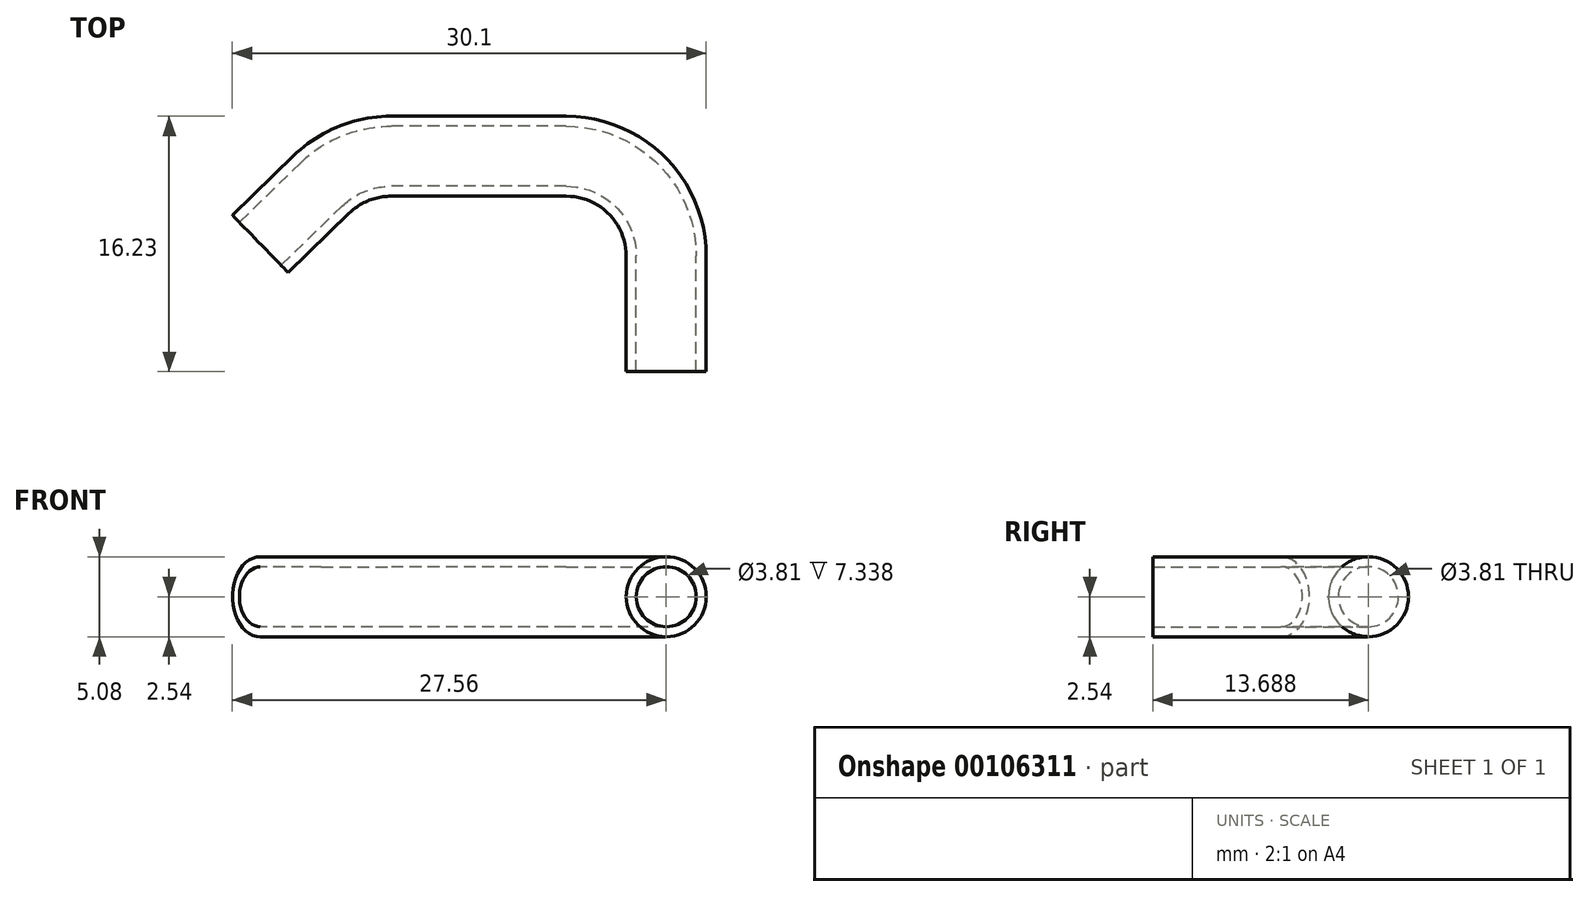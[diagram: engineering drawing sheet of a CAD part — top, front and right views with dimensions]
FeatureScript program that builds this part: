
annotation { "Feature Type Name" : "Feature", "Feature Type Description" : "" }
export const myFeature = defineFeature(function(context is Context, id is Id, definition is map)
    precondition{}
    {
        {
            var Q0;
            Q0=qCreatedBy(makeId("Front.planeOp"),FACE);
            var sketch = newSketch(context, id + "F0", { "sketchPlane" : qUnion([Q0])});
            skCircle(sketch, "E0", {"center": v(0, 0) * mm, "radius": 2.54 * mm});
            skCircle(sketch, "E1", {"center": v(0, 0) * mm, "radius": 1.9 * mm});
            skSolve(sketch);
        }
        {
            var Q0;
            Q0=qCreatedBy(makeId("Top.planeOp"),FACE);
            var sketch = newSketch(context, id + "F1", { "sketchPlane" : qUnion([Q0])});
            skLineSegment(sketch, "E2", {"start": v(0, 0) * mm, "end": v(0, 7.34) * mm});
            skLineSegment(sketch, "E3", {"start": v(-6.35, 13.69) * mm, "end": v(-12.53, 13.69) * mm});
            skPoint(sketch, "E4.visualSharp", {"position": v(0, 13.69) * mm});
            skArc(sketch, "E4.filletArc", {"start": v(0, 7.34) * mm, "mid": v(-1.86, 11.83) * mm, "end": v(-6.35, 13.69) * mm});
            skLineSegment(sketch, "E5", {"start": v(-12.53, 13.69) * mm, "end": v(-17.49, 13.69) * mm});
            skLineSegment(sketch, "E6", {"start": v(-21.9, 11.9) * mm, "end": v(-25.79, 8.13) * mm});
            skPoint(sketch, "E7.visualSharp", {"position": v(-20.06, 13.69) * mm});
            skArc(sketch, "E7.filletArc", {"start": v(-17.49, 13.69) * mm, "mid": v(-19.87, 13.22) * mm, "end": v(-21.9, 11.9) * mm});
            skSolve(sketch);
        }
        {
            var Q0;
            Q0 = qSketchRegion(id + "F0", true);
            var Q1;
            Q1 = qConstructionFilter(qBodyType(qCreatedBy(id + "F1" ,EDGE), BodyType.WIRE), ConstructionObject.NO);
            sweep(context, id + "F2", {"profiles" : qUnion([Q0]), "path" : qUnion([Q1])});
        }
    });
